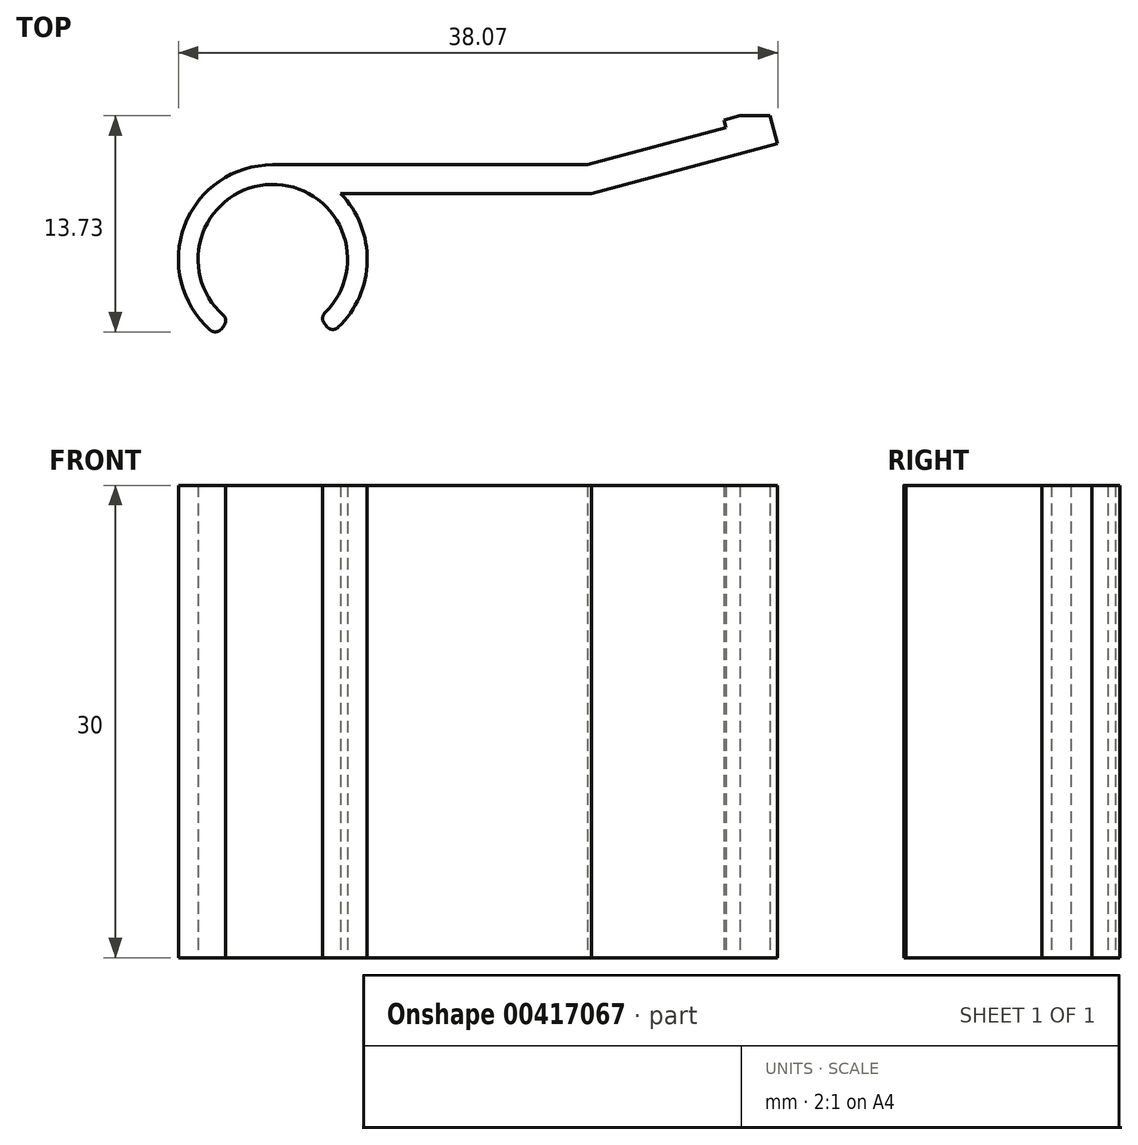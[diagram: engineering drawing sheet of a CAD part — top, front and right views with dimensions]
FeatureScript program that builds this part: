
annotation { "Feature Type Name" : "Feature", "Feature Type Description" : "" }
export const myFeature = defineFeature(function(context is Context, id is Id, definition is map)
    precondition{}
    {
        {
            var Q0;
            Q0=qCreatedBy(makeId("Top.planeOp"),FACE);
            var sketch = newSketch(context, id + "F0", { "sketchPlane" : qUnion([Q0])});
            skArc(sketch, "E0", {"start": v(2.99, -3.7) * mm, "mid": v(-0.12, 4.75) * mm, "end": v(-2.8, -3.84) * mm});
            skArc(sketch, "E1", {"start": v(3.73, -4.7) * mm, "mid": v(-0.1, 6) * mm, "end": v(-3.57, -4.82) * mm});
            skLineSegment(sketch, "E2", {"start": v(0, 6) * mm, "end": v(20, 6) * mm});
            skLineSegment(sketch, "E3", {"start": v(20, 6) * mm, "end": v(31.6, 9.1) * mm});
            skLineSegment(sketch, "E4.0", {"start": v(20.24, 4.17) * mm, "end": v(32.07, 7.34) * mm});
            skLineSegment(sketch, "E4.1", {"start": v(2.28, 4.17) * mm, "end": v(20.24, 4.17) * mm});
            skLineSegment(sketch, "E5", {"start": v(31.6, 9.1) * mm, "end": v(32.07, 7.34) * mm});
            skLineSegment(sketch, "E6", {"start": v(31.6, 9.1) * mm, "end": v(29.68, 9.1) * mm});
            skLineSegment(sketch, "E7", {"start": v(29.68, 9.1) * mm, "end": v(28.66, 8.83) * mm});
            skLineSegment(sketch, "E8", {"start": v(28.66, 8.83) * mm, "end": v(28.79, 8.35) * mm});
            skLineSegment(sketch, "E9", {"start": v(-2.8, -3.84) * mm, "end": v(-3.57, -4.82) * mm});
            skLineSegment(sketch, "E10", {"start": v(2.99, -3.7) * mm, "end": v(3.73, -4.7) * mm});
            skSolve(sketch);
        }
        {
            var Q0;
            Q0=qSketchRegion(id+"F0",true);
            extrude(context, id + "F1", {"entities" : qUnion([Q0]), "depth" : 30 * mm, "offsetDistance" : 25 * mm});
        }
        {
            var Q0;
            Q0=makeQuery(id+"F1.opExtrude","SWEPT_EDGE",EDGE,{"disambiguationData":[OSD([sQuery(id+"F0.wireOp",EDGE,"E1"),sQuery(id+"F0.wireOp",EDGE,"E9")])]});
            var Q1;
            Q1=makeQuery(id+"F1.opExtrude","SWEPT_EDGE",EDGE,{"disambiguationData":[OSD([sQuery(id+"F0.wireOp",EDGE,"E0"),sQuery(id+"F0.wireOp",EDGE,"E9")])]});
            var Q2;
            Q2=makeQuery(id+"F1.opExtrude","SWEPT_EDGE",EDGE,{"disambiguationData":[OSD([sQuery(id+"F0.wireOp",EDGE,"E1"),sQuery(id+"F0.wireOp",EDGE,"E10")])]});
            var Q3;
            Q3=makeQuery(id+"F1.opExtrude","SWEPT_EDGE",EDGE,{"disambiguationData":[OSD([sQuery(id+"F0.wireOp",EDGE,"E0"),sQuery(id+"F0.wireOp",EDGE,"E10")])]});
            fillet(context, id + "F2", {"entities" : qUnion([Q0, Q1, Q2, Q3]), "radius" : .5 * mm, "tangentPropagation" : true, "allowEdgeOverflow" : false});
        }
    });
